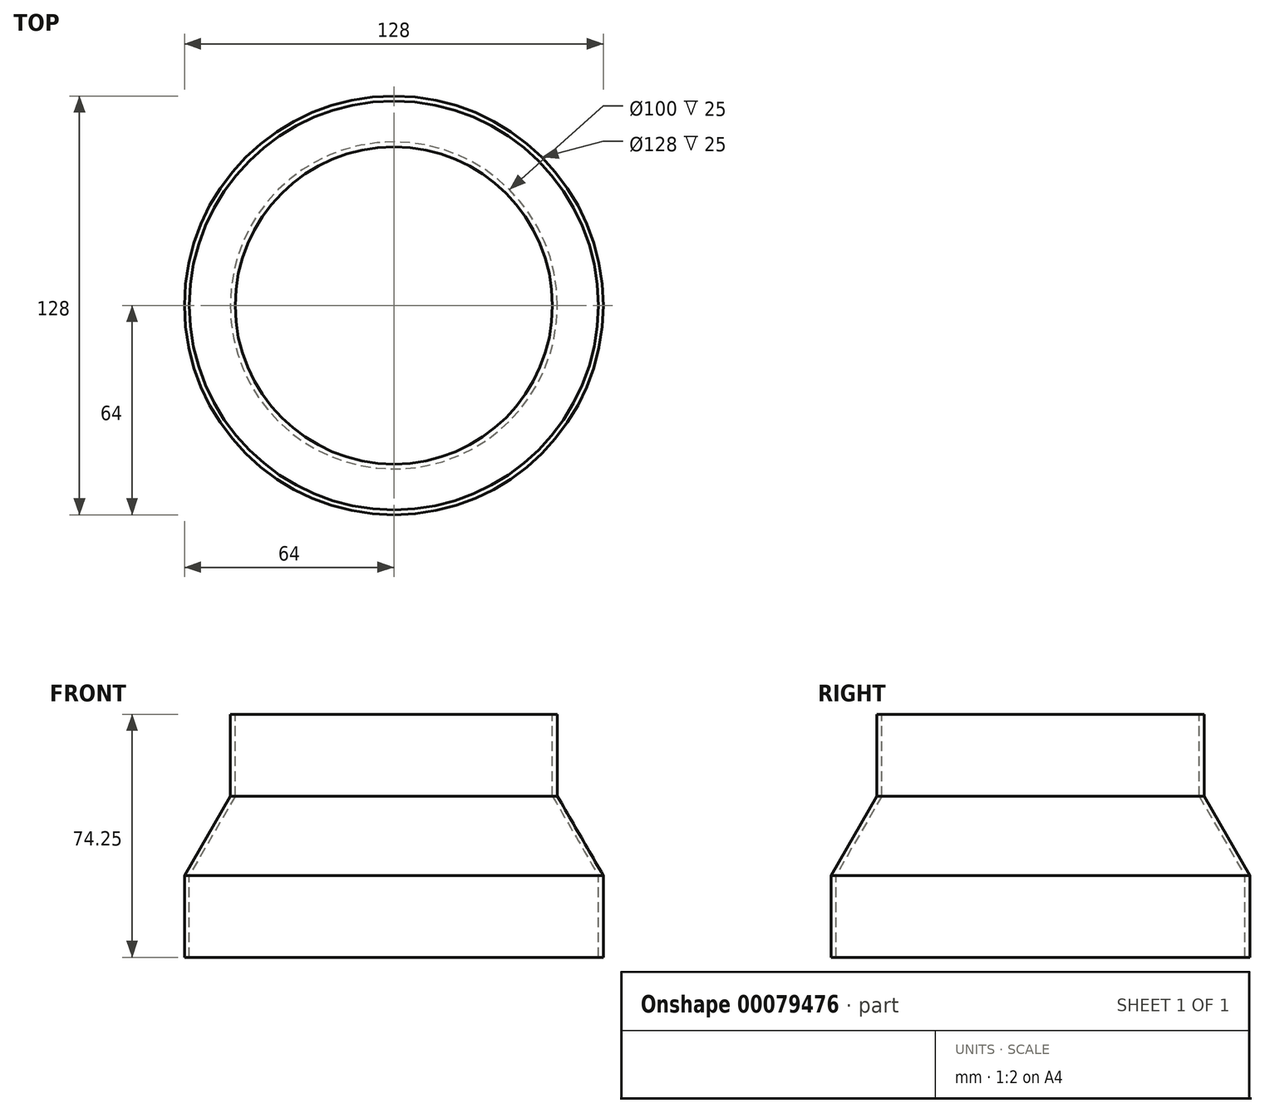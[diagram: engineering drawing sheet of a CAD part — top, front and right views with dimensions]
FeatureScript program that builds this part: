
annotation { "Feature Type Name" : "Feature", "Feature Type Description" : "" }
export const myFeature = defineFeature(function(context is Context, id is Id, definition is map)
    precondition{}
    {
        {
            var Q0;
            Q0=qCreatedBy(makeId("Right.planeOp"),FACE);
            var sketch = newSketch(context, id + "F0", { "sketchPlane" : qUnion([Q0])});
            skLineSegment(sketch, "E0", {"start": v(-64, 0) * mm, "end": v(-64, 25) * mm});
            skLineSegment(sketch, "E1", {"start": v(-64, 25) * mm, "end": v(-50, 49.25) * mm});
            skLineSegment(sketch, "E2", {"start": v(-50, 49.25) * mm, "end": v(-50, 74.25) * mm});
            skLineSegment(sketch, "E3", {"start": v(-50, 74.25) * mm, "end": v(-48.5, 74.25) * mm});
            skLineSegment(sketch, "E4", {"start": v(-48.5, 74.25) * mm, "end": v(-48.5, 49.25) * mm});
            skLineSegment(sketch, "E5", {"start": v(-48.5, 49.25) * mm, "end": v(-62.5, 25) * mm});
            skLineSegment(sketch, "E6", {"start": v(-62.5, 25) * mm, "end": v(-62.5, 0) * mm});
            skLineSegment(sketch, "E7", {"start": v(-62.5, 0) * mm, "end": v(-64, 0) * mm});
            skLineSegment(sketch, "E8", {"start": v(-64, 0) * mm, "end": v(0, 0) * mm, "construction": true});
            skLineSegment(sketch, "E9", {"start": v(0, 0) * mm, "end": v(0, 128.28) * mm, "construction": true});
            skSolve(sketch);
        }
        {
            var Q0;
            Q0 = qConstructionFilter(qBodyType(qCreatedBy(id + "F0" ,EDGE), BodyType.WIRE), ConstructionObject.NO);
            var Q1;
            Q1=sQuery(id+"F0.wireOp",EDGE,"E9");
            revolve(context, id + "F1", {"bodyType" : ExtendedToolBodyType.SURFACE, "surfaceOperationType" : NewSurfaceOperationType.NEW, "surfaceEntities" : qUnion([Q0]), "axis" : qUnion([Q1]), "revolveType" : RevolveType.FULL});
        }
    });
